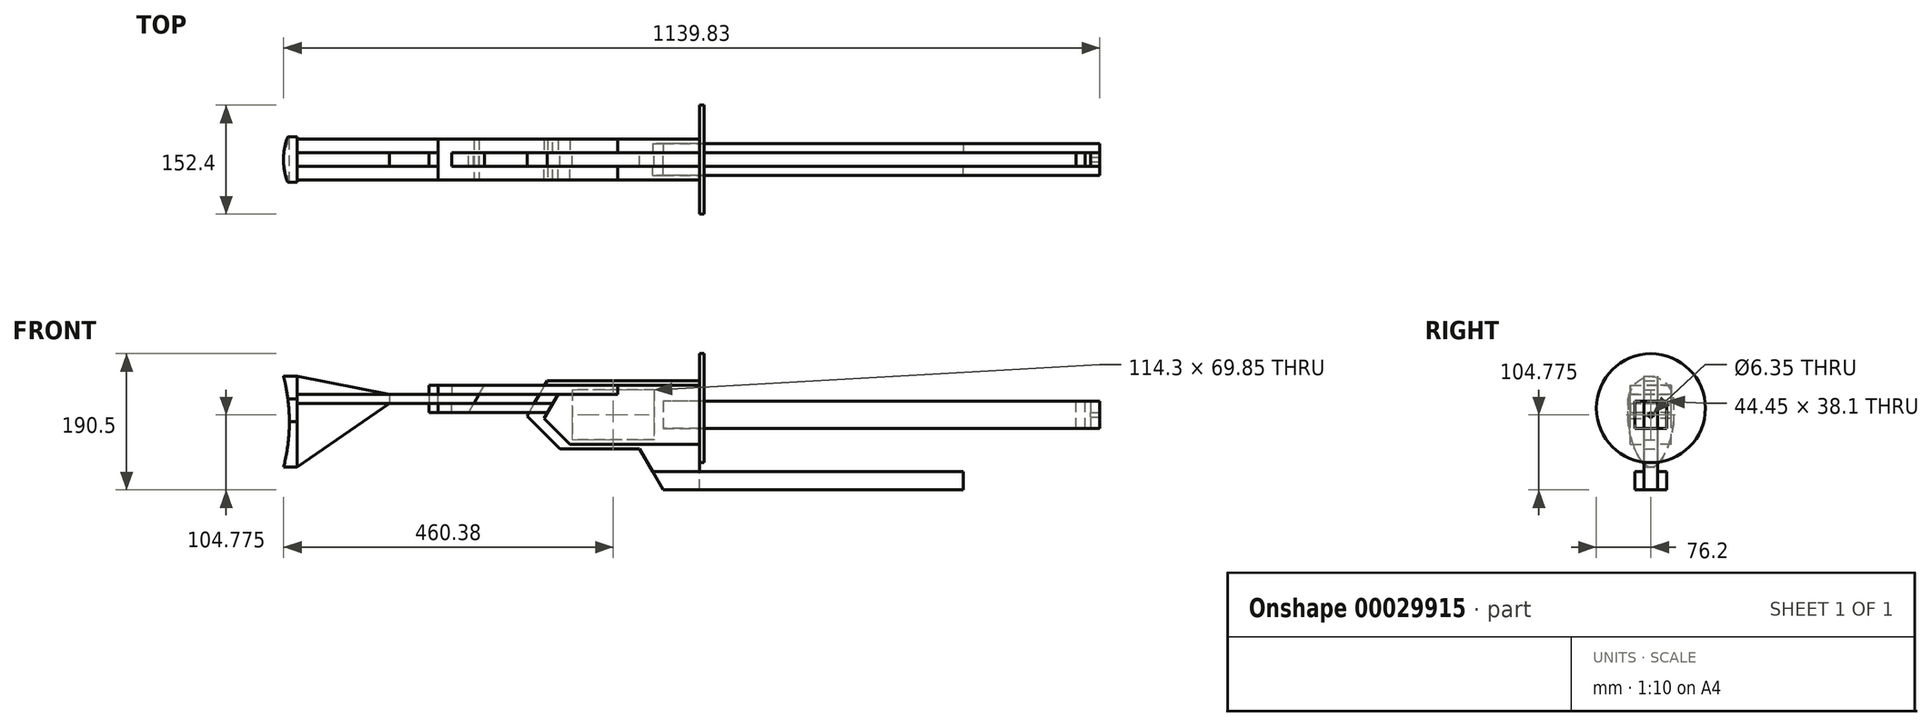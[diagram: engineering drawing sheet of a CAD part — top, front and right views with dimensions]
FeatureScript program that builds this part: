
annotation { "Feature Type Name" : "Feature", "Feature Type Description" : "" }
export const myFeature = defineFeature(function(context is Context, id is Id, definition is map)
    precondition{}
    {
        {
            var Q0;
            Q0=qCreatedBy(makeId("Front.planeOp"),FACE);
            var sketch = newSketch(context, id + "F0", { "sketchPlane" : qUnion([Q0])});
            skLineSegment(sketch, "E0", {"start": v(0, 0) * mm, "end": v(-212.72, 0) * mm});
            skLineSegment(sketch, "E1", {"start": v(-212.72, 0) * mm, "end": v(-241.07, -49.1) * mm});
            skLineSegment(sketch, "E2", {"start": v(-241.07, -49.1) * mm, "end": v(-194.92, -95.25) * mm});
            skLineSegment(sketch, "E3", {"start": v(-194.92, -95.25) * mm, "end": v(-83.8, -95.25) * mm});
            skLineSegment(sketch, "E4", {"start": v(-83.8, -95.25) * mm, "end": v(-50.8, -152.4) * mm});
            skLineSegment(sketch, "E5", {"start": v(-50.8, -152.4) * mm, "end": v(0, -152.4) * mm});
            skLineSegment(sketch, "E6", {"start": v(0, -152.4) * mm, "end": v(0, 0) * mm});
            skLineSegment(sketch, "E7.bottom", {"start": v(-63.5, -12.7) * mm, "end": v(-177.8, -12.7) * mm});
            skLineSegment(sketch, "E7.top", {"start": v(-63.5, -82.55) * mm, "end": v(-177.8, -82.55) * mm});
            skLineSegment(sketch, "E7.left", {"start": v(-63.5, -12.7) * mm, "end": v(-63.5, -82.55) * mm});
            skLineSegment(sketch, "E7.right", {"start": v(-177.8, -12.7) * mm, "end": v(-177.8, -82.55) * mm});
            skSolve(sketch);
        }
        {
            var Q0;
            Q0 = qSketchRegion(id + "F0", true);
            extrude(context, id + "F1", {"entities" : qUnion([Q0]), "endBound" : BoundingType.SYMMETRIC, "depth" : 19.05 * mm});
        }
        {
            var Q0;
            Q0=makeQuery(id+"F1.opExtrude","CAP_FACE",FACE,{"disambiguationData":[OSD([sQuery(id+"F0.wireOp",EDGE,"E0"),sQuery(id+"F0.wireOp",EDGE,"E1"),sQuery(id+"F0.wireOp",EDGE,"E2"),sQuery(id+"F0.wireOp",EDGE,"E3"),sQuery(id+"F0.wireOp",EDGE,"E4"),sQuery(id+"F0.wireOp",EDGE,"E5"),sQuery(id+"F0.wireOp",EDGE,"E6"),sQuery(id+"F0.wireOp",EDGE,"E7.bottom"),sQuery(id+"F0.wireOp",EDGE,"E7.top"),sQuery(id+"F0.wireOp",EDGE,"E7.left"),sQuery(id+"F0.wireOp",EDGE,"E7.right")])],"isStart":false});
            var sketch = newSketch(context, id + "F2", { "sketchPlane" : qUnion([Q0])});
            skLineSegment(sketch, "E8", {"start": v(0, -6.35) * mm, "end": v(0, -88.9) * mm});
            skLineSegment(sketch, "E9", {"start": v(0, -88.9) * mm, "end": v(-180.98, -88.9) * mm});
            skLineSegment(sketch, "E10", {"start": v(-180.98, -88.9) * mm, "end": v(-217.23, -52.65) * mm});
            skLineSegment(sketch, "E11", {"start": v(-217.23, -52.65) * mm, "end": v(-190.5, -6.35) * mm});
            skLineSegment(sketch, "E12", {"start": v(-190.5, -6.35) * mm, "end": v(0, -6.35) * mm});
            skLineSegment(sketch, "E13", {"start": v(-114.3, -6.35) * mm, "end": v(-114.3, -19.05) * mm});
            skLineSegment(sketch, "E14", {"start": v(-114.3, -19.05) * mm, "end": v(-197.83, -19.05) * mm});
            skSolve(sketch);
        }
        {
            var Q0;
            {var subQ3=makeQuery(id+"F1.opExtrude","CAP_EDGE",EDGE,{"disambiguationData":[OSD([sQuery(id+"F0.wireOp",EDGE,"E7.top")])],"isStart":false});Q0=makeQuery(id+"F2.imprint","IMPRINT",FACE,{"disambiguationData":[TD([[makeQuery(id+"F2.imprint","IMPRINT",EDGE,{"derivedFrom":subQ3}),-1.0]])]});}
            var Q1;
            {var subQ13=sQuery(id+"F2.wireOp",EDGE,"E8");Q1=makeQuery(id+"F2.imprint","IMPRINT",FACE,{"disambiguationData":[TD([[makeQuery(id+"F2.imprint","IMPRINT",EDGE,{"derivedFrom":subQ13}),1.0]])]});}
            extrude(context, id + "F3", {"entities" : qUnion([Q0, Q1]), "depth" : 19.05 * mm});
        }
        {
            var Q0;
            Q0=makeQuery(id+"F3.opExtrude","CAP_FACE",FACE,{"disambiguationData":[OSD([sQuery(id+"F2.wireOp",EDGE,"E8"),sQuery(id+"F2.wireOp",EDGE,"E9"),sQuery(id+"F2.wireOp",EDGE,"E10"),sQuery(id+"F2.wireOp",EDGE,"E11"),sQuery(id+"F2.wireOp",EDGE,"E12"),sQuery(id+"F2.wireOp",EDGE,"E13"),sQuery(id+"F2.wireOp",EDGE,"E14")])],"isStart":true});
            var sketch = newSketch(context, id + "F4", { "sketchPlane" : qUnion([Q0])});
            skLineSegment(sketch, "E15.bottom", {"start": v(0, -28.58) * mm, "end": v(50.8, -28.58) * mm});
            skLineSegment(sketch, "E15.top", {"start": v(0, -66.68) * mm, "end": v(50.8, -66.68) * mm});
            skLineSegment(sketch, "E15.left", {"start": v(0, -28.58) * mm, "end": v(0, -66.68) * mm});
            skLineSegment(sketch, "E15.right", {"start": v(50.8, -28.57) * mm, "end": v(50.8, -66.68) * mm});
            skLineSegment(sketch, "E16", {"start": v(50.8, -47.62) * mm, "end": v(0, -47.62) * mm, "construction": true});
            skSolve(sketch);
        }
        {
            var Q0;
            Q0 = qSketchRegion(id + "F4", true);
            extrude(context, id + "F5", {"entities" : qUnion([Q0]), "operationType" : NewBodyOperationType.REMOVE, "oppositeDirection" : true, "depth" : 12.7 * mm});
        }
        {
            var Q0;
            Q0=makeQuery(id+"F3.opExtrude","SWEPT_BODY",BODY,{"disambiguationData":[OSD([sQuery(id+"F2.wireOp",EDGE,"E8"),sQuery(id+"F2.wireOp",EDGE,"E9"),sQuery(id+"F2.wireOp",EDGE,"E10"),sQuery(id+"F2.wireOp",EDGE,"E11"),sQuery(id+"F2.wireOp",EDGE,"E12"),sQuery(id+"F2.wireOp",EDGE,"E13"),sQuery(id+"F2.wireOp",EDGE,"E14")])]});
            var Q1;
            Q1=qCreatedBy(makeId("Front.planeOp"),FACE);
            mirror(context, id + "F6", {"entities" : qUnion([Q0]), "mirrorPlane" : qUnion([Q1])});
        }
        {
            var Q0;
            Q0=makeQuery(id+"F6.opPattern","COPY",FACE,{"derivedFrom":makeQuery(id+"F3.opExtrude","SWEPT_FACE",FACE,{"disambiguationData":[OSD([sQuery(id+"F2.wireOp",EDGE,"E14")])]}),"instanceName":"1"});
            var sketch = newSketch(context, id + "F7", { "sketchPlane" : qUnion([Q0])});
            skLineSegment(sketch, "E17", {"start": v(-114.3, 28.58) * mm, "end": v(-114.3, 9.53) * mm});
            skLineSegment(sketch, "E18", {"start": v(-114.3, 9.53) * mm, "end": v(-346.08, 9.52) * mm});
            skLineSegment(sketch, "E19", {"start": v(-346.08, 9.52) * mm, "end": v(-346.08, -9.53) * mm});
            skLineSegment(sketch, "E20", {"start": v(-346.08, -9.53) * mm, "end": v(-114.3, -9.53) * mm});
            skLineSegment(sketch, "E21", {"start": v(-114.3, -9.53) * mm, "end": v(-114.3, -28.58) * mm});
            skLineSegment(sketch, "E22", {"start": v(-114.3, -28.58) * mm, "end": v(-365.13, -28.58) * mm});
            skLineSegment(sketch, "E23", {"start": v(-365.13, -28.58) * mm, "end": v(-365.13, 28.58) * mm});
            skLineSegment(sketch, "E24", {"start": v(-365.13, 28.58) * mm, "end": v(-114.3, 28.58) * mm});
            skSolve(sketch);
        }
        {
            var Q0;
            Q0 = qSketchRegion(id + "F7", true);
            extrude(context, id + "F8", {"entities" : qUnion([Q0]), "depth" : 12.7 * mm});
        }
        {
            var Q0;
            Q0=makeQuery(id+"F8.opExtrude","CAP_FACE",FACE,{"disambiguationData":[OSD([sQuery(id+"F7.wireOp",EDGE,"E17"),sQuery(id+"F7.wireOp",EDGE,"E18"),sQuery(id+"F7.wireOp",EDGE,"E19"),sQuery(id+"F7.wireOp",EDGE,"E20"),sQuery(id+"F7.wireOp",EDGE,"E21"),sQuery(id+"F7.wireOp",EDGE,"E22"),sQuery(id+"F7.wireOp",EDGE,"E23"),sQuery(id+"F7.wireOp",EDGE,"E24")])],"isStart":true});
            var sketch = newSketch(context, id + "F9", { "sketchPlane" : qUnion([Q0])});
            skLineSegment(sketch, "E25", {"start": v(-365.13, 9.53) * mm, "end": v(-365.13, -9.52) * mm});
            skLineSegment(sketch, "E26", {"start": v(-365.13, -9.52) * mm, "end": v(-561.98, -9.52) * mm});
            skLineSegment(sketch, "E27", {"start": v(-561.98, -9.52) * mm, "end": v(-561.98, -28.58) * mm});
            skLineSegment(sketch, "E28", {"start": v(-561.98, -28.58) * mm, "end": v(-307.98, -28.58) * mm});
            skLineSegment(sketch, "E29", {"start": v(-307.98, -28.58) * mm, "end": v(-307.98, 28.58) * mm});
            skLineSegment(sketch, "E30", {"start": v(-307.98, 28.58) * mm, "end": v(-561.98, 28.58) * mm});
            skLineSegment(sketch, "E31", {"start": v(-561.98, 28.58) * mm, "end": v(-561.98, 9.53) * mm});
            skLineSegment(sketch, "E32", {"start": v(-561.98, 9.53) * mm, "end": v(-365.13, 9.53) * mm});
            skSolve(sketch);
        }
        {
            var Q0;
            Q0 = qSketchRegion(id + "F9", true);
            extrude(context, id + "F10", {"entities" : qUnion([Q0]), "depth" : 12.7 * mm});
        }
        {
            var Q0;
            Q0=makeQuery(id+"F10.opExtrude","CAP_EDGE",EDGE,{"disambiguationData":[OSD([sQuery(id+"F9.wireOp",EDGE,"E29")])],"isStart":false});
            chamfer(context, id + "F11", {"entities" : qUnion([Q0]), "chamferType" : ChamferType.OFFSET_ANGLE, "width" : 12.7 * mm, "oppositeDirection" : true, "angle" : 30 * degree, "tangentPropagation" : true});
        }
        {
            var Q0;
            Q0=makeQuery(id+"F10.opExtrude","CAP_FACE",FACE,{"disambiguationData":[OSD([sQuery(id+"F9.wireOp",EDGE,"E25"),sQuery(id+"F9.wireOp",EDGE,"E26"),sQuery(id+"F9.wireOp",EDGE,"E27"),sQuery(id+"F9.wireOp",EDGE,"E28"),sQuery(id+"F9.wireOp",EDGE,"E29"),sQuery(id+"F9.wireOp",EDGE,"E30"),sQuery(id+"F9.wireOp",EDGE,"E31"),sQuery(id+"F9.wireOp",EDGE,"E32")])],"isStart":false});
            var sketch = newSketch(context, id + "F12", { "sketchPlane" : qUnion([Q0])});
            skLineSegment(sketch, "E33.bottom", {"start": v(-365.13, 28.58) * mm, "end": v(-205.16, 28.58) * mm});
            skLineSegment(sketch, "E33.top", {"start": v(-365.13, -28.58) * mm, "end": v(-205.16, -28.58) * mm});
            skLineSegment(sketch, "E33.left", {"start": v(-365.13, 28.58) * mm, "end": v(-365.13, -28.58) * mm});
            skLineSegment(sketch, "E34", {"start": v(-205.16, 28.58) * mm, "end": v(-205.16, 9.53) * mm});
            skLineSegment(sketch, "E35", {"start": v(-205.16, 9.53) * mm, "end": v(-346.08, 9.53) * mm});
            skLineSegment(sketch, "E36", {"start": v(-346.08, 9.53) * mm, "end": v(-346.08, -9.52) * mm});
            skLineSegment(sketch, "E37", {"start": v(-346.08, -9.52) * mm, "end": v(-205.16, -9.52) * mm});
            skLineSegment(sketch, "E38", {"start": v(-205.16, -9.52) * mm, "end": v(-205.16, -28.57) * mm});
            skSolve(sketch);
        }
        {
            var Q0;
            Q0 = qSketchRegion(id + "F12", true);
            extrude(context, id + "F13", {"entities" : qUnion([Q0]), "depth" : 12.7 * mm});
        }
        {
            var Q0;
            Q0=makeQuery(id+"F13.opExtrude","CAP_EDGE",EDGE,{"disambiguationData":[OSD([sQuery(id+"F12.wireOp",EDGE,"E34")])],"isStart":false});
            var Q1;
            Q1=makeQuery(id+"F13.opExtrude","CAP_EDGE",EDGE,{"disambiguationData":[OSD([sQuery(id+"F12.wireOp",EDGE,"E38")])],"isStart":false});
            chamfer(context, id + "F14", {"entities" : qUnion([Q0, Q1]), "chamferType" : ChamferType.OFFSET_ANGLE, "width" : 12.7 * mm, "oppositeDirection" : false, "angle" : 30 * degree, "tangentPropagation" : true});
        }
        {
            var Q0;
            Q0=makeQuery(id+"F1.opExtrude","SWEPT_FACE",FACE,{"disambiguationData":[OSD([sQuery(id+"F0.wireOp",EDGE,"E6")])]});
            var sketch = newSketch(context, id + "F15", { "sketchPlane" : qUnion([Q0])});
            skCircle(sketch, "E39", {"center": v(0, -38.1) * mm, "radius": 76.2 * mm});
            skLineSegment(sketch, "E40.rect.bottom", {"start": v(22.22, -28.58) * mm, "end": v(-22.22, -28.58) * mm});
            skLineSegment(sketch, "E40.rect.top", {"start": v(22.23, -66.68) * mm, "end": v(-22.22, -66.68) * mm});
            skLineSegment(sketch, "E40.rect.left", {"start": v(22.23, -28.58) * mm, "end": v(22.23, -66.68) * mm});
            skLineSegment(sketch, "E40.rect.right", {"start": v(-22.22, -28.58) * mm, "end": v(-22.22, -66.68) * mm});
            skPoint(sketch, "E40.rect.middle", {"position": v(0, -47.63) * mm});
            skLineSegment(sketch, "E41", {"start": v(0, -28.58) * mm, "end": v(0, -38.1) * mm, "construction": true});
            skSolve(sketch);
        }
        {
            var Q0;
            Q0 = qSketchRegion(id + "F15", true);
            extrude(context, id + "F16", {"entities" : qUnion([Q0]), "depth" : 6.35 * mm});
        }
        {
            var Q0;
            {var subQ1=sQuery(id+"F4.wireOp",EDGE,"E15.bottom");Q0=makeQuery(id+"F4.imprint","IMPRINT",FACE,{"disambiguationData":[TD([[makeQuery(id+"F4.imprint","IMPRINT",EDGE,{"derivedFrom":subQ1}),1.0]])]});}
            var sketch = newSketch(context, id + "F17", { "sketchPlane" : qUnion([Q0])});
            skLineSegment(sketch, "E42.bottom", {"start": v(50.8, -28.58) * mm, "end": v(-558.8, -28.58) * mm});
            skLineSegment(sketch, "E42.top", {"start": v(50.8, -66.68) * mm, "end": v(-558.8, -66.68) * mm});
            skLineSegment(sketch, "E42.left", {"start": v(50.8, -28.58) * mm, "end": v(50.8, -66.68) * mm});
            skLineSegment(sketch, "E42.right", {"start": v(-558.8, -28.58) * mm, "end": v(-558.8, -66.68) * mm});
            skSolve(sketch);
        }
        {
            var Q0;
            Q0 = qSketchRegion(id + "F17", true);
            extrude(context, id + "F18", {"entities" : qUnion([Q0]), "oppositeDirection" : true, "depth" : 12.7 * mm});
        }
        {
            var Q0;
            Q0=makeQuery(id+"F18.opExtrude","SWEPT_BODY",BODY,{"disambiguationData":[OSD([sQuery(id+"F17.wireOp",EDGE,"E42.bottom"),sQuery(id+"F17.wireOp",EDGE,"E42.top"),sQuery(id+"F17.wireOp",EDGE,"E42.left"),sQuery(id+"F17.wireOp",EDGE,"E42.right")])]});
            var Q1;
            Q1=qCreatedBy(makeId("Front.planeOp"),FACE);
            mirror(context, id + "F19", {"entities" : qUnion([Q0]), "mirrorPlane" : qUnion([Q1])});
        }
        {
            var Q0;
            Q0=makeQuery(id+"F1.opExtrude","CAP_FACE",FACE,{"disambiguationData":[OSD([sQuery(id+"F0.wireOp",EDGE,"E0"),sQuery(id+"F0.wireOp",EDGE,"E1"),sQuery(id+"F0.wireOp",EDGE,"E2"),sQuery(id+"F0.wireOp",EDGE,"E3"),sQuery(id+"F0.wireOp",EDGE,"E4"),sQuery(id+"F0.wireOp",EDGE,"E5"),sQuery(id+"F0.wireOp",EDGE,"E6"),sQuery(id+"F0.wireOp",EDGE,"E7.bottom"),sQuery(id+"F0.wireOp",EDGE,"E7.top"),sQuery(id+"F0.wireOp",EDGE,"E7.left"),sQuery(id+"F0.wireOp",EDGE,"E7.right")])],"isStart":false});
            var sketch = newSketch(context, id + "F20", { "sketchPlane" : qUnion([Q0])});
            skLineSegment(sketch, "E43", {"start": v(-50.8, -152.4) * mm, "end": v(368.3, -152.4) * mm});
            skLineSegment(sketch, "E44", {"start": v(368.3, -152.4) * mm, "end": v(368.3, -127) * mm});
            skLineSegment(sketch, "E45", {"start": v(368.3, -127) * mm, "end": v(-65.46, -127) * mm});
            skLineSegment(sketch, "E46", {"start": v(-65.46, -127) * mm, "end": v(-50.8, -152.4) * mm});
            skSolve(sketch);
        }
        {
            var Q0;
            Q0 = qSketchRegion(id + "F20", true);
            extrude(context, id + "F21", {"entities" : qUnion([Q0]), "depth" : 12.7 * mm});
        }
        {
            var Q0;
            Q0=makeQuery(id+"F21.opExtrude","SWEPT_BODY",BODY,{"disambiguationData":[OSD([sQuery(id+"F20.wireOp",EDGE,"E43"),sQuery(id+"F20.wireOp",EDGE,"E44"),sQuery(id+"F20.wireOp",EDGE,"E45"),sQuery(id+"F20.wireOp",EDGE,"E46")])]});
            var Q1;
            Q1=qCreatedBy(makeId("Front.planeOp"),FACE);
            mirror(context, id + "F22", {"entities" : qUnion([Q0]), "mirrorPlane" : qUnion([Q1])});
        }
        {
            var Q0;
            Q0=makeQuery(id+"F8.opExtrude","SWEPT_FACE",FACE,{"disambiguationData":[OSD([sQuery(id+"F7.wireOp",EDGE,"E18")])]});
            var sketch = newSketch(context, id + "F23", { "sketchPlane" : qUnion([Q0])});
            skLineSegment(sketch, "E47", {"start": v(-346.08, -19.05) * mm, "end": v(-307.98, -19.05) * mm});
            skLineSegment(sketch, "E48", {"start": v(-307.98, -19.05) * mm, "end": v(-300.64, -6.35) * mm});
            skLineSegment(sketch, "E49", {"start": v(-300.64, -6.35) * mm, "end": v(-346.08, -6.35) * mm});
            skLineSegment(sketch, "E50", {"start": v(-346.08, -6.35) * mm, "end": v(-346.08, -19.05) * mm});
            skLineSegment(sketch, "E51", {"start": v(-346.08, -31.75) * mm, "end": v(-315.6, -31.75) * mm});
            skLineSegment(sketch, "E52", {"start": v(-315.6, -31.75) * mm, "end": v(-322.93, -44.45) * mm});
            skLineSegment(sketch, "E53", {"start": v(-322.93, -44.45) * mm, "end": v(-346.08, -44.45) * mm});
            skLineSegment(sketch, "E54", {"start": v(-346.08, -44.45) * mm, "end": v(-346.08, -31.75) * mm});
            skSolve(sketch);
        }
        {
            var Q0;
            Q0 = qSketchRegion(id + "F23", true);
            extrude(context, id + "F24", {"entities" : qUnion([Q0]), "depth" : 19.05 * mm});
        }
        {
            var Q0;
            Q0=makeQuery(id+"F8.opExtrude","SWEPT_FACE",FACE,{"disambiguationData":[OSD([sQuery(id+"F7.wireOp",EDGE,"E23")])]});
            var sketch = newSketch(context, id + "F25", { "sketchPlane" : qUnion([Q0])});
            skLineSegment(sketch, "E55.bottom", {"start": v(-9.53, -6.35) * mm, "end": v(9.53, -6.35) * mm});
            skLineSegment(sketch, "E55.top", {"start": v(-9.53, -44.45) * mm, "end": v(9.53, -44.45) * mm});
            skLineSegment(sketch, "E55.left", {"start": v(-9.53, -6.35) * mm, "end": v(-9.53, -44.45) * mm});
            skLineSegment(sketch, "E55.right", {"start": v(9.53, -6.35) * mm, "end": v(9.53, -44.45) * mm});
            skSolve(sketch);
        }
        {
            var Q0;
            Q0 = qSketchRegion(id + "F25", true);
            extrude(context, id + "F26", {"entities" : qUnion([Q0]), "depth" : 12.7 * mm});
        }
        {
            var Q0;
            Q0=makeQuery(id+"F10.opExtrude","SWEPT_FACE",FACE,{"disambiguationData":[OSD([sQuery(id+"F9.wireOp",EDGE,"E27")])]});
            var sketch = newSketch(context, id + "F27", { "sketchPlane" : qUnion([Q0])});
            skLineSegment(sketch, "E56", {"start": v(-9.52, -25.4) * mm, "end": v(9.53, -25.4) * mm, "construction": true});
            skLineSegment(sketch, "E57.bottom", {"start": v(-31.75, 6.35) * mm, "end": v(31.75, 6.35) * mm});
            skLineSegment(sketch, "E57.top", {"start": v(-31.75, -120.65) * mm, "end": v(31.75, -120.65) * mm});
            skLineSegment(sketch, "E57.left", {"start": v(-31.75, 6.35) * mm, "end": v(-31.75, -120.65) * mm});
            skLineSegment(sketch, "E57.right", {"start": v(31.75, 6.35) * mm, "end": v(31.75, -120.65) * mm});
            skLineSegment(sketch, "E58", {"start": v(0, -25.4) * mm, "end": v(0, 6.35) * mm, "construction": true});
            skFitSpline(sketch, "E59", {"points": [v(-31.75, -25.4) * mm, v(0, 6.35) * mm, v(31.75, -25.4) * mm], "startDerivative": vector(19.05, 114.3) * mm, "endDerivative": vector(19.05, -114.3) * mm});
            skLineSegment(sketch, "E60", {"start": v(0, -120.65) * mm, "end": v(0, -57.15) * mm, "construction": true});
            skFitSpline(sketch, "E61", {"points": [v(31.75, -57.15) * mm, v(0, -120.65) * mm, v(-31.75, -57.15) * mm], "startDerivative": vector(-19.05, -190.5) * mm, "endDerivative": vector(-19.05, 190.5) * mm});
            skSolve(sketch);
        }
        {
            var Q0;
            {var subQ0=sQuery(id+"F9.wireOp",EDGE,"E27");Q0=makeQuery(id+"F27.imprint","IMPRINT",FACE,{"disambiguationData":[TD([[makeQuery(id+"F27.imprint","IMPRINT",EDGE,{"derivedFrom":makeQuery(id+"F10.opExtrude","CAP_EDGE",EDGE,{"disambiguationData":[OSD([subQ0])],"isStart":true})}),1.0]])]});}
            var Q1;
            {var subQ0=sQuery(id+"F9.wireOp",EDGE,"E27");Q1=makeQuery(id+"F27.imprint","IMPRINT",FACE,{"disambiguationData":[TD([[makeQuery(id+"F27.imprint","IMPRINT",EDGE,{"derivedFrom":makeQuery(id+"F10.opExtrude","CAP_EDGE",EDGE,{"disambiguationData":[OSD([subQ0])],"isStart":true})}),-1.0]])]});}
            extrude(context, id + "F28", {"entities" : qUnion([Q0, Q1]), "depth" : 19.05 * mm});
        }
        {
            var Q0;
            Q0=makeQuery(id+"F10.opExtrude","SWEPT_FACE",FACE,{"disambiguationData":[OSD([sQuery(id+"F9.wireOp",EDGE,"E26")])]});
            var sketch = newSketch(context, id + "F29", { "sketchPlane" : qUnion([Q0])});
            skLineSegment(sketch, "E62", {"start": v(-561.98, 6.35) * mm, "end": v(-432.94, -19.05) * mm});
            skLineSegment(sketch, "E63", {"start": v(-432.94, -19.05) * mm, "end": v(-432.94, -31.75) * mm});
            skLineSegment(sketch, "E64", {"start": v(-432.94, -31.75) * mm, "end": v(-561.98, -120.65) * mm});
            skLineSegment(sketch, "E65", {"start": v(-561.98, -120.65) * mm, "end": v(-561.98, 6.35) * mm});
            skSolve(sketch);
        }
        {
            var Q0;
            Q0 = qSketchRegion(id + "F29", true);
            extrude(context, id + "F30", {"entities" : qUnion([Q0]), "depth" : 19.05 * mm});
        }
        {
            var Q0;
            Q0=makeQuery(id+"F28.opExtrude","SWEPT_FACE",FACE,{"disambiguationData":[OSD([sQuery(id+"F27.wireOp",EDGE,"E57.left")])]});
            var sketch = newSketch(context, id + "F31", { "sketchPlane" : qUnion([Q0])});
            skLineSegment(sketch, "E66", {"start": v(581.02, 6.35) * mm, "end": v(581.02, -120.65) * mm});
            skCircle(sketch, "E67", {"center": v(826.96, -57.15) * mm, "radius": 254 * mm});
            skPoint(sketch, "E67.third.point", {"position": v(1068.34, -136.23) * mm});
            skSolve(sketch);
        }
        {
            var Q0;
            Q0 = qSketchRegion(id + "F31", true);
            extrude(context, id + "F32", {"entities" : qUnion([Q0]), "operationType" : NewBodyOperationType.REMOVE, "endBound" : BoundingType.THROUGH_ALL, "oppositeDirection" : true, "depth" : 25.4 * mm});
        }
        {
            var Q0;
            Q0=makeQuery(id+"F19.opPattern","COPY",FACE,{"derivedFrom":makeQuery(id+"F18.opExtrude","CAP_FACE",FACE,{"disambiguationData":[OSD([sQuery(id+"F17.wireOp",EDGE,"E42.bottom"),sQuery(id+"F17.wireOp",EDGE,"E42.top"),sQuery(id+"F17.wireOp",EDGE,"E42.left"),sQuery(id+"F17.wireOp",EDGE,"E42.right")])],"isStart":true}),"instanceName":"1"});
            var sketch = newSketch(context, id + "F33", { "sketchPlane" : qUnion([Q0])});
            skLineSegment(sketch, "E68.bottom", {"start": v(558.8, -28.58) * mm, "end": v(546.1, -28.58) * mm});
            skLineSegment(sketch, "E68.top", {"start": v(558.8, -66.68) * mm, "end": v(546.1, -66.68) * mm});
            skLineSegment(sketch, "E68.left", {"start": v(558.8, -28.58) * mm, "end": v(558.8, -66.68) * mm});
            skLineSegment(sketch, "E68.right", {"start": v(546.1, -28.58) * mm, "end": v(546.1, -66.68) * mm});
            skLineSegment(sketch, "E69.bottom", {"start": v(538.48, -66.68) * mm, "end": v(525.78, -66.68) * mm});
            skLineSegment(sketch, "E69.top", {"start": v(538.48, -28.58) * mm, "end": v(525.78, -28.58) * mm});
            skLineSegment(sketch, "E69.left", {"start": v(538.48, -66.68) * mm, "end": v(538.48, -28.58) * mm});
            skLineSegment(sketch, "E69.right", {"start": v(525.78, -66.68) * mm, "end": v(525.78, -28.58) * mm});
            skSolve(sketch);
        }
        {
            var Q0;
            Q0 = qSketchRegion(id + "F33", true);
            extrude(context, id + "F34", {"entities" : qUnion([Q0]), "depth" : 19.05 * mm});
        }
        {
            var Q0;
            Q0=makeQuery(id+"F34.opExtrude","SWEPT_FACE",FACE,{"disambiguationData":[OSD([sQuery(id+"F33.wireOp",EDGE,"E68.left")])]});
            var sketch = newSketch(context, id + "F35", { "sketchPlane" : qUnion([Q0])});
            skLineSegment(sketch, "E70", {"start": v(9.53, -28.57) * mm, "end": v(-9.53, -66.67) * mm, "construction": true});
            skCircle(sketch, "E71", {"center": v(0, -47.62) * mm, "radius": 3.18 * mm});
            skSolve(sketch);
        }
        {
            var Q0;
            Q0 = qSketchRegion(id + "F35", true);
            extrude(context, id + "F36", {"entities" : qUnion([Q0]), "operationType" : NewBodyOperationType.REMOVE, "oppositeDirection" : true, "depth" : 12.7 * mm});
        }
    });
